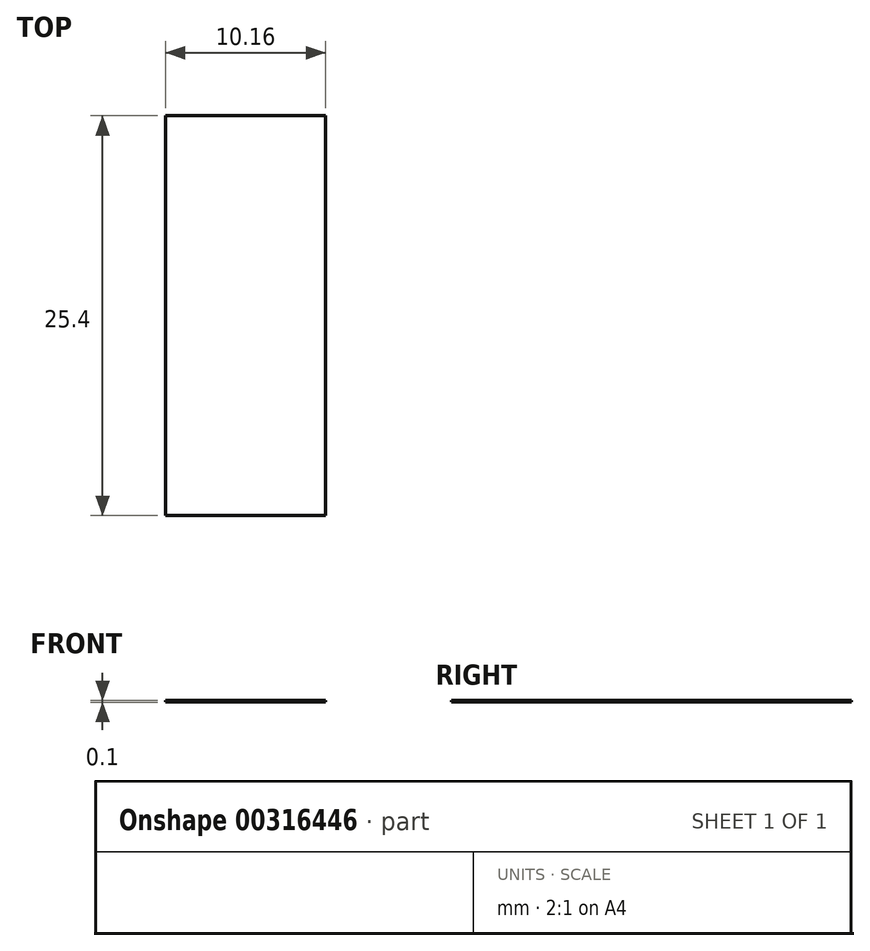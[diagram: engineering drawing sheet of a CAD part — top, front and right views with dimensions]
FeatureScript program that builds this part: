
annotation { "Feature Type Name" : "Feature", "Feature Type Description" : "" }
export const myFeature = defineFeature(function(context is Context, id is Id, definition is map)
    precondition{}
    {
        {
            var Q0;
            Q0=qCreatedBy(makeId("Front.planeOp"),FACE);
            var sketch = newSketch(context, id + "F0", { "sketchPlane" : qUnion([Q0])});
            skLineSegment(sketch, "E0.bottom", {"start": v(-5019.6, -6.84) * mm, "end": v(-5009.45, -6.84) * mm});
            skLineSegment(sketch, "E0.top", {"start": v(-5019.6, -6.94) * mm, "end": v(-5009.45, -6.94) * mm});
            skLineSegment(sketch, "E0.left", {"start": v(-5019.6, -6.84) * mm, "end": v(-5019.6, -6.94) * mm});
            skLineSegment(sketch, "E0.right", {"start": v(-5009.45, -6.84) * mm, "end": v(-5009.45, -6.94) * mm});
            skSolve(sketch);
        }
        {
            var Q0;
            Q0=makeQuery(id+"F0.imprint","IMPRINT",FACE,{"disambiguationData":[TD([[makeQuery(id+"F0.imprint","IMPRINT",EDGE,{"derivedFrom":sQuery(id+"F0.wireOp",EDGE,"E0.bottom")}),-1.0]])]});
            extrude(context, id + "F1", {"entities" : qUnion([Q0]), "depth" : 25.4 * mm});
        }
    });
